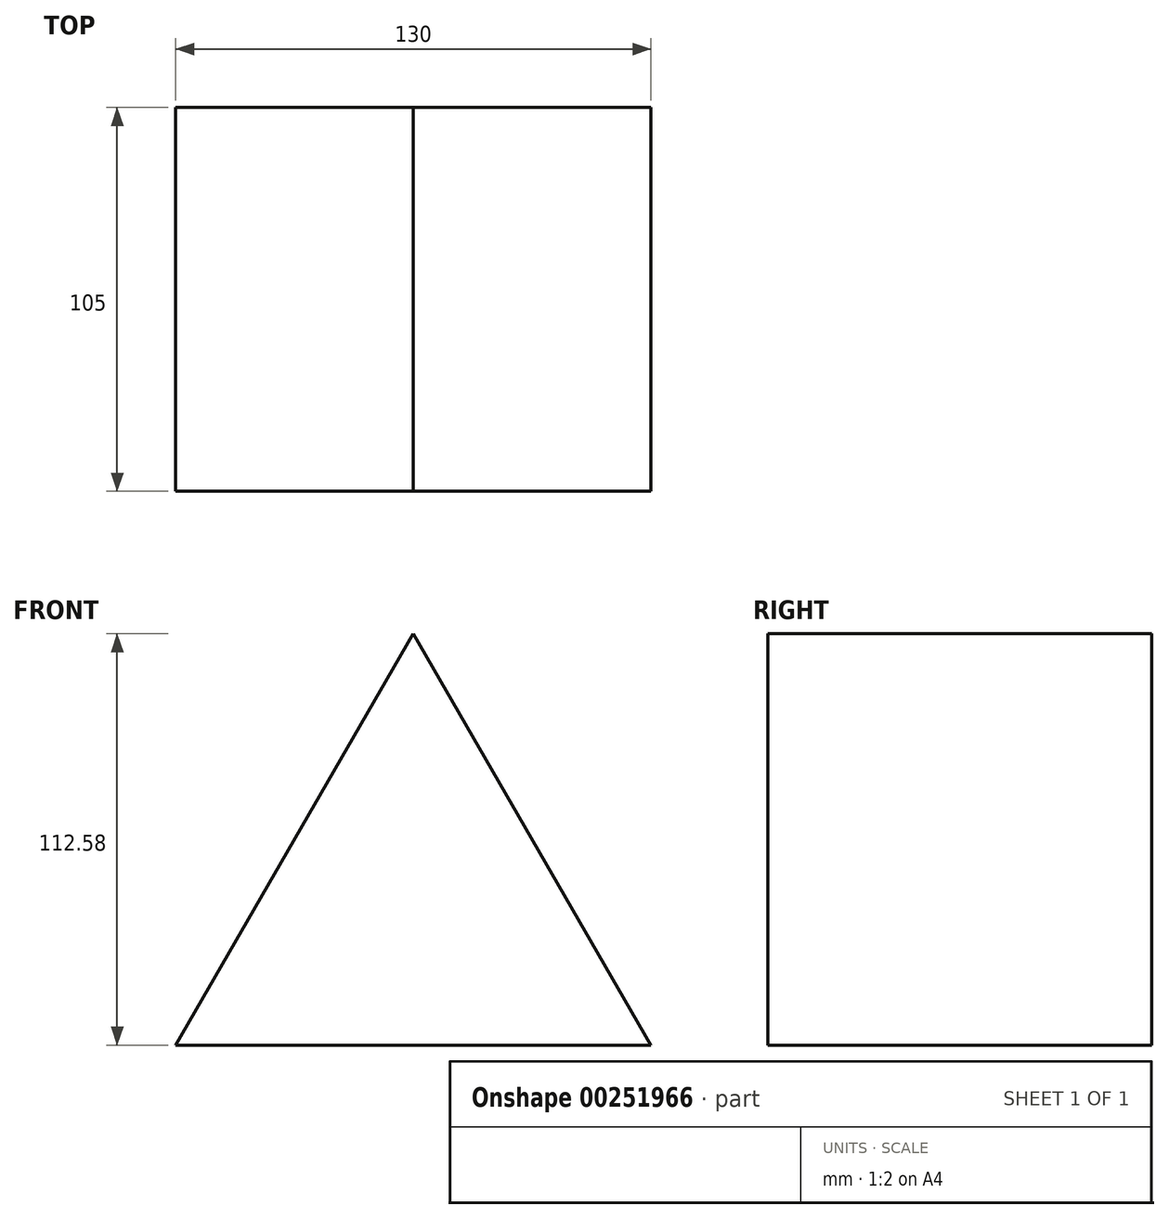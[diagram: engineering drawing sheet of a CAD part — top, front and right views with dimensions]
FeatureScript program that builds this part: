
annotation { "Feature Type Name" : "Feature", "Feature Type Description" : "" }
export const myFeature = defineFeature(function(context is Context, id is Id, definition is map)
    precondition{}
    {
        {
            var Q0;
            Q0=qCreatedBy(makeId("Front.planeOp"),FACE);
            var sketch = newSketch(context, id + "F0", { "sketchPlane" : qUnion([Q0])});
            skLineSegment(sketch, "E0", {"start": v(-58.14, -74.28) * mm, "end": v(71.86, -74.28) * mm});
            skLineSegment(sketch, "E1", {"start": v(71.86, -74.28) * mm, "end": v(6.86, 38.3) * mm});
            skLineSegment(sketch, "E2", {"start": v(6.86, 38.3) * mm, "end": v(-58.14, -74.28) * mm});
            skLineSegment(sketch, "E3.0", {"start": v(63.2, -69.28) * mm, "end": v(6.86, 28.3) * mm});
            skLineSegment(sketch, "E3.1", {"start": v(-49.48, -69.28) * mm, "end": v(63.2, -69.28) * mm});
            skLineSegment(sketch, "E3.2", {"start": v(6.86, 28.3) * mm, "end": v(-49.48, -69.28) * mm});
            skSolve(sketch);
        }
        {
            var Q0;
            Q0=makeQuery(id+"F0.imprint","IMPRINT",FACE,{"disambiguationData":[TD([[makeQuery(id+"F0.imprint","IMPRINT",EDGE,{"derivedFrom":sQuery(id+"F0.wireOp",EDGE,"E0")}),1.0]])]});
            extrude(context, id + "F1", {"entities" : qUnion([Q0]), "depth" : 105 * mm});
        }
        {
            var Q0;
            Q0=makeQuery(id+"F0.imprint","IMPRINT",FACE,{"disambiguationData":[TD([[makeQuery(id+"F0.imprint","IMPRINT",EDGE,{"derivedFrom":sQuery(id+"F0.wireOp",EDGE,"E3.0")}),1.0]])]});
            extrude(context, id + "F2", {"entities" : qUnion([Q0]), "operationType" : NewBodyOperationType.ADD, "depth" : 105 * mm});
        }
    });
